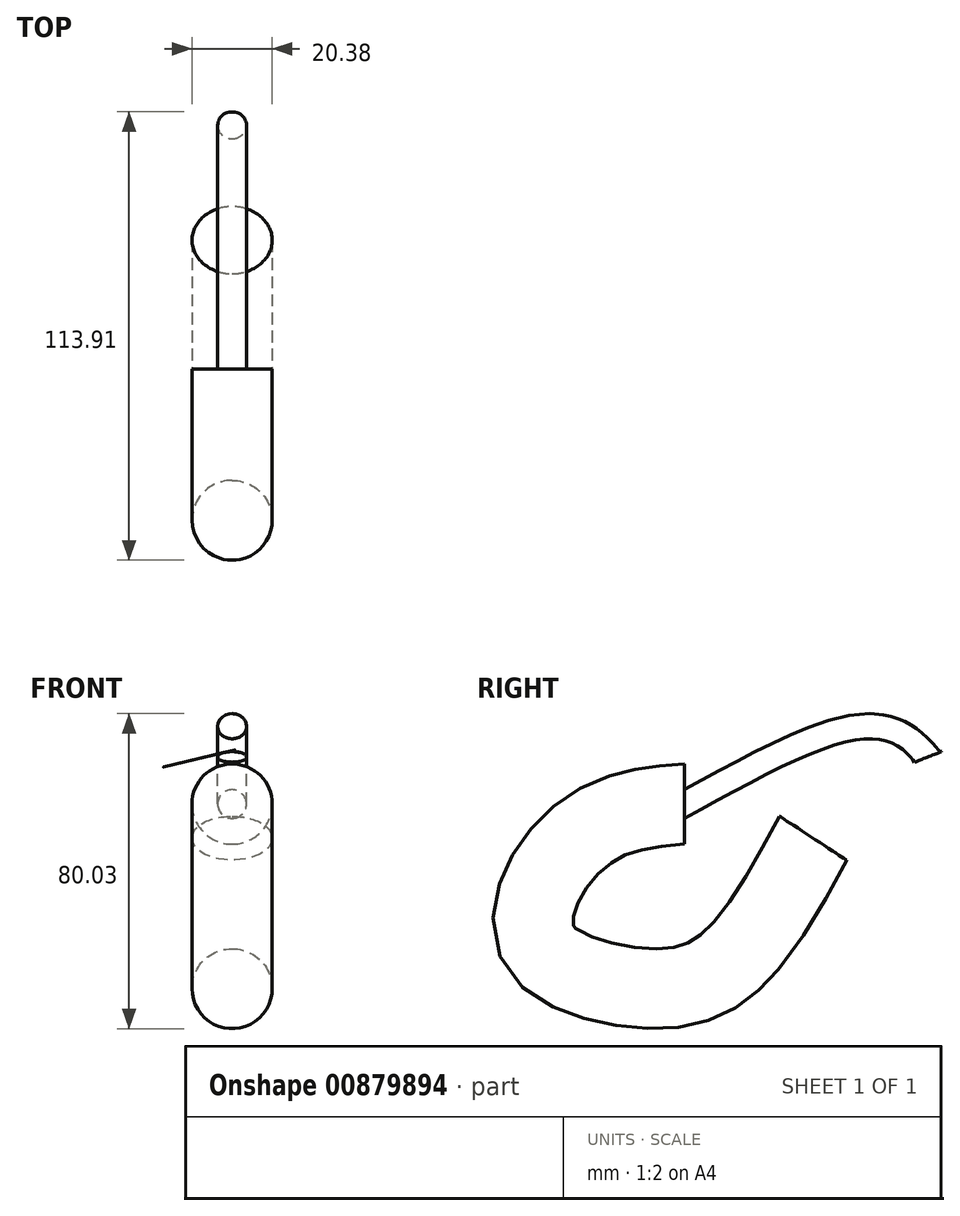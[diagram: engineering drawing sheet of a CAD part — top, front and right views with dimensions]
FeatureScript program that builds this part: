
annotation { "Feature Type Name" : "Feature", "Feature Type Description" : "" }
export const myFeature = defineFeature(function(context is Context, id is Id, definition is map)
    precondition{}
    {
        {
            var Q0;
            Q0=qCreatedBy(makeId("Front.planeOp"),FACE);
            var sketch = newSketch(context, id + "F0", { "sketchPlane" : qUnion([Q0])});
            skCircle(sketch, "E0", {"center": v(0, 0) * mm, "radius": 3.66 * mm});
            skSolve(sketch);
        }
        {
            var Q0;
            Q0=qCreatedBy(makeId("Right.planeOp"),FACE);
            var sketch = newSketch(context, id + "F1", { "sketchPlane" : qUnion([Q0])});
            skFitSpline(sketch, "E1", {"points": [v(0, 0) * mm, v(43.17, 19.42) * mm, v(56.74, 16.73) * mm, v(61.42, 12.4) * mm, v(61.88, 11.97) * mm], "startDerivative": vector(97.9, 54.06) * mm, "endDerivative": vector(6.37, -5.27) * mm});
            skSolve(sketch);
        }
        {
            var Q0;
            Q0=makeQuery(id+"F0.imprint","IMPRINT",FACE,{"disambiguationData":[TD([[makeQuery(id+"F0.imprint","IMPRINT",EDGE,{"derivedFrom":sQuery(id+"F0.wireOp",EDGE,"E0")}),1.0]])]});
            var Q1;
            Q1=sQuery(id+"F1.wireOp",EDGE,"E1");
            sweep(context, id + "F2", {"profiles" : qUnion([Q0]), "path" : qUnion([Q1])});
        }
        {
            var Q0;
            Q0=qCreatedBy(makeId("Front.planeOp"),FACE);
            var sketch = newSketch(context, id + "F3", { "sketchPlane" : qUnion([Q0])});
            skCircle(sketch, "E2", {"center": v(0, 0) * mm, "radius": 10.19 * mm});
            skSolve(sketch);
        }
        {
            var Q0;
            Q0=qCreatedBy(makeId("Right.planeOp"),FACE);
            var sketch = newSketch(context, id + "F4", { "sketchPlane" : qUnion([Q0])});
            skFitSpline(sketch, "E3", {"points": [v(0, 0) * mm, v(-21.46, -4.79) * mm, v(-36.77, -21.92) * mm, v(-35.86, -37.46) * mm, v(-12.55, -46.6) * mm, v(9.6, -41.8) * mm, v(32.68, -8.67) * mm], "startDerivative": vector(-140.7, -11.73) * mm, "endDerivative": vector(100.73, 186.43) * mm});
            skSolve(sketch);
        }
        {
            var Q0;
            Q0=makeQuery(id+"F3.imprint","IMPRINT",FACE,{"disambiguationData":[TD([[makeQuery(id+"F3.imprint","IMPRINT",EDGE,{"derivedFrom":sQuery(id+"F3.wireOp",EDGE,"E2")}),1.0]])]});
            var Q1;
            Q1=sQuery(id+"F4.wireOp",EDGE,"E3");
            sweep(context, id + "F5", {"operationType" : NewBodyOperationType.ADD, "profiles" : qUnion([Q0]), "path" : qUnion([Q1])});
        }
    });
